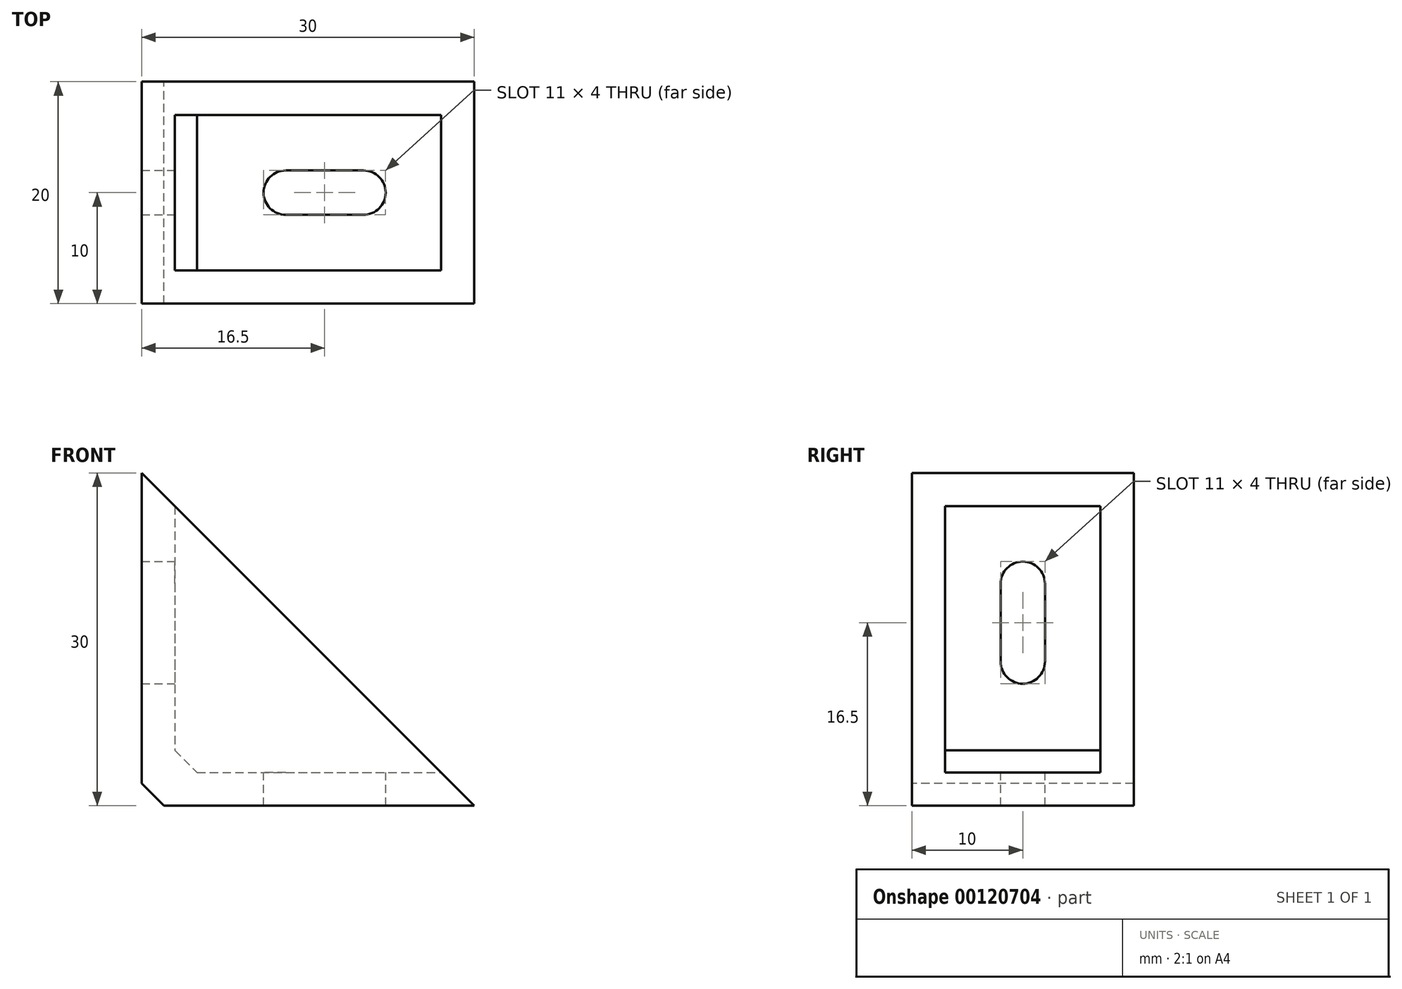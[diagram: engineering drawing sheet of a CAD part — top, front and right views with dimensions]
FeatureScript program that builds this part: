
annotation { "Feature Type Name" : "Feature", "Feature Type Description" : "" }
export const myFeature = defineFeature(function(context is Context, id is Id, definition is map)
    precondition{}
    {
        {
            var Q0;
            Q0=qCreatedBy(makeId("Front.planeOp"),FACE);
            var sketch = newSketch(context, id + "F0", { "sketchPlane" : qUnion([Q0])});
            skLineSegment(sketch, "E0", {"start": v(0, 0) * mm, "end": v(30, 0) * mm});
            skLineSegment(sketch, "E1", {"start": v(30, 0) * mm, "end": v(0, 30) * mm});
            skLineSegment(sketch, "E2", {"start": v(0, 30) * mm, "end": v(0, 0) * mm});
            skSolve(sketch);
        }
        {
            var Q0;
            Q0 = qSketchRegion(id + "F0", true);
            extrude(context, id + "F1", {"entities" : qUnion([Q0]), "depth" : 20 * mm});
        }
        {
            var Q0;
            Q0=qCreatedBy(makeId("Front.planeOp"),FACE);
            var sketch = newSketch(context, id + "F2", { "sketchPlane" : qUnion([Q0])});
            skLineSegment(sketch, "E3", {"start": v(3, 28.88) * mm, "end": v(3, 3) * mm});
            skLineSegment(sketch, "E4", {"start": v(3, 3) * mm, "end": v(29.66, 3) * mm});
            skLineSegment(sketch, "E5", {"start": v(29.66, 3) * mm, "end": v(3, 28.88) * mm});
            skSolve(sketch);
        }
        {
            var Q0;
            Q0 = qSketchRegion(id + "F2", true);
            extrude(context, id + "F3", {"entities" : qUnion([Q0]), "operationType" : NewBodyOperationType.REMOVE, "depth" : 17 * mm});
        }
        {
            var Q0;
            Q0=makeQuery(id+"F1.opExtrude","CAP_FACE",FACE,{"disambiguationData":[OSD([sQuery(id+"F0.wireOp",EDGE,"E0"),sQuery(id+"F0.wireOp",EDGE,"E1"),sQuery(id+"F0.wireOp",EDGE,"E2")])],"isStart":true});
            var sketch = newSketch(context, id + "F4", { "sketchPlane" : qUnion([Q0])});
            skLineSegment(sketch, "E6", {"start": v(-3, 27) * mm, "end": v(-3, 3) * mm});
            skLineSegment(sketch, "E7", {"start": v(-3, 3) * mm, "end": v(-27, 3) * mm});
            skLineSegment(sketch, "E8", {"start": v(-27, 3) * mm, "end": v(-3, 27) * mm});
            skSolve(sketch);
        }
        {
            var Q0;
            Q0 = qSketchRegion(id + "F4", true);
            extrude(context, id + "F5", {"entities" : qUnion([Q0]), "operationType" : NewBodyOperationType.ADD, "oppositeDirection" : true, "depth" : 3 * mm});
        }
        {
            var Q0;
            Q0=makeQuery(id+"F1.opExtrude","SWEPT_EDGE",EDGE,{"disambiguationData":[OSD([sQuery(id+"F0.wireOp",EDGE,"E0"),sQuery(id+"F0.wireOp",EDGE,"E2")])]});
            chamfer(context, id + "F6", {"entities" : qUnion([Q0]), "width" : 2 * mm, "tangentPropagation" : true});
        }
        {
            var Q0;
            Q0=makeQuery(id+"F3.boolean.opBoolean","COPY",FACE,{"derivedFrom":makeQuery(id+"F3.opExtrude","SWEPT_FACE",FACE,{"disambiguationData":[OSD([sQuery(id+"F2.wireOp",EDGE,"E3")])]})});
            var sketch = newSketch(context, id + "F7", { "sketchPlane" : qUnion([Q0])});
            skLineSegment(sketch, "E9", {"start": v(-10, 27) * mm, "end": v(-10, 3) * mm, "construction": true});
            skCircle(sketch, "E10", {"center": v(-10, 20) * mm, "radius": 2 * mm});
            skCircle(sketch, "E11", {"center": v(-10, 13) * mm, "radius": 2 * mm});
            skLineSegment(sketch, "E12", {"start": v(-8, 20) * mm, "end": v(-8, 13) * mm});
            skLineSegment(sketch, "E13", {"start": v(-12, 20) * mm, "end": v(-12, 13) * mm});
            skSolve(sketch);
        }
        {
            var Q0;
            Q0 = qSketchRegion(id + "F7", true);
            extrude(context, id + "F8", {"entities" : qUnion([Q0]), "operationType" : NewBodyOperationType.REMOVE, "oppositeDirection" : true, "depth" : 25 * mm});
        }
        {
            var Q0;
            Q0=makeQuery(id+"F3.boolean.opBoolean","COPY",EDGE,{"derivedFrom":makeQuery(id+"F3.opExtrude","SWEPT_EDGE",EDGE,{"disambiguationData":[OSD([sQuery(id+"F2.wireOp",EDGE,"E3"),sQuery(id+"F2.wireOp",EDGE,"E4")])]})});
            chamfer(context, id + "F9", {"entities" : qUnion([Q0]), "width" : 2 * mm, "tangentPropagation" : true});
        }
        {
            var Q0;
            Q0=makeQuery(id+"F3.boolean.opBoolean","COPY",FACE,{"derivedFrom":makeQuery(id+"F3.opExtrude","SWEPT_FACE",FACE,{"disambiguationData":[OSD([sQuery(id+"F2.wireOp",EDGE,"E4")])]})});
            var sketch = newSketch(context, id + "F10", { "sketchPlane" : qUnion([Q0])});
            skLineSegment(sketch, "E14", {"start": v(5, -10) * mm, "end": v(27, -10) * mm, "construction": true});
            skCircle(sketch, "E15", {"center": v(20, -10) * mm, "radius": 2 * mm});
            skCircle(sketch, "E16", {"center": v(13, -10) * mm, "radius": 2 * mm});
            skLineSegment(sketch, "E17", {"start": v(13, -8) * mm, "end": v(20, -8) * mm});
            skLineSegment(sketch, "E18", {"start": v(13, -12) * mm, "end": v(20, -12) * mm});
            skSolve(sketch);
        }
        {
            var Q0;
            Q0 = qSketchRegion(id + "F10", true);
            extrude(context, id + "F11", {"entities" : qUnion([Q0]), "operationType" : NewBodyOperationType.REMOVE, "oppositeDirection" : true, "depth" : 25 * mm});
        }
    });
